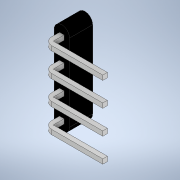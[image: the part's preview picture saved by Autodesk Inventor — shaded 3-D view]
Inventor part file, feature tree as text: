
AUTODESK INVENTOR PART (.ipt)
format: ipt  version: 2021 (Build 250183000, 183)  size: 182,272 bytes
history: native  units: mm
features: extrude x3, sketch x3, other x1, fillet x1, pattern_linear x1
ambient origin geometry x8: Origin, YZ Plane, XZ Plane, XY Plane, X Axis, Y Axis, Z Axis, Center Point
bodies: Body1 (feature_tree)
feature tree (9):
  other  "Sólido1"
  extrude  "Extrusão1"  Depth=2.0mm
  extrude  "Extrusão2"  Depth=0.6mm
  extrude  "Extrusão3"  Depth=0.6mm
  fillet  "Arredondamento1"  Radius=0.3mm
  pattern_linear  "Padrão retangular1"  Spacing1=2.0mm  [1 undecoded]
  sketch  "Esboço1"  dims[d0=10.0mm d1=2.0mm]
  sketch  "Esboço2"  dims[d2=3.0mm d3=0.0mm d4=0.6mm]
  sketch  "Esboço3"  dims[d5=0.6mm d6=0.6mm d7=0.3mm d8=2.0mm d9=0.0mm d13=7.0mm d14=0.6mm d15=0.0mm d16=1.0mm d17=40.0mm d19=3.1333mm]
note: 1 required parameter value undecoded (feature->parameter linkage not recoverable at this tier; creation-order binding heuristic only, values carry confidence <= 0.55)
